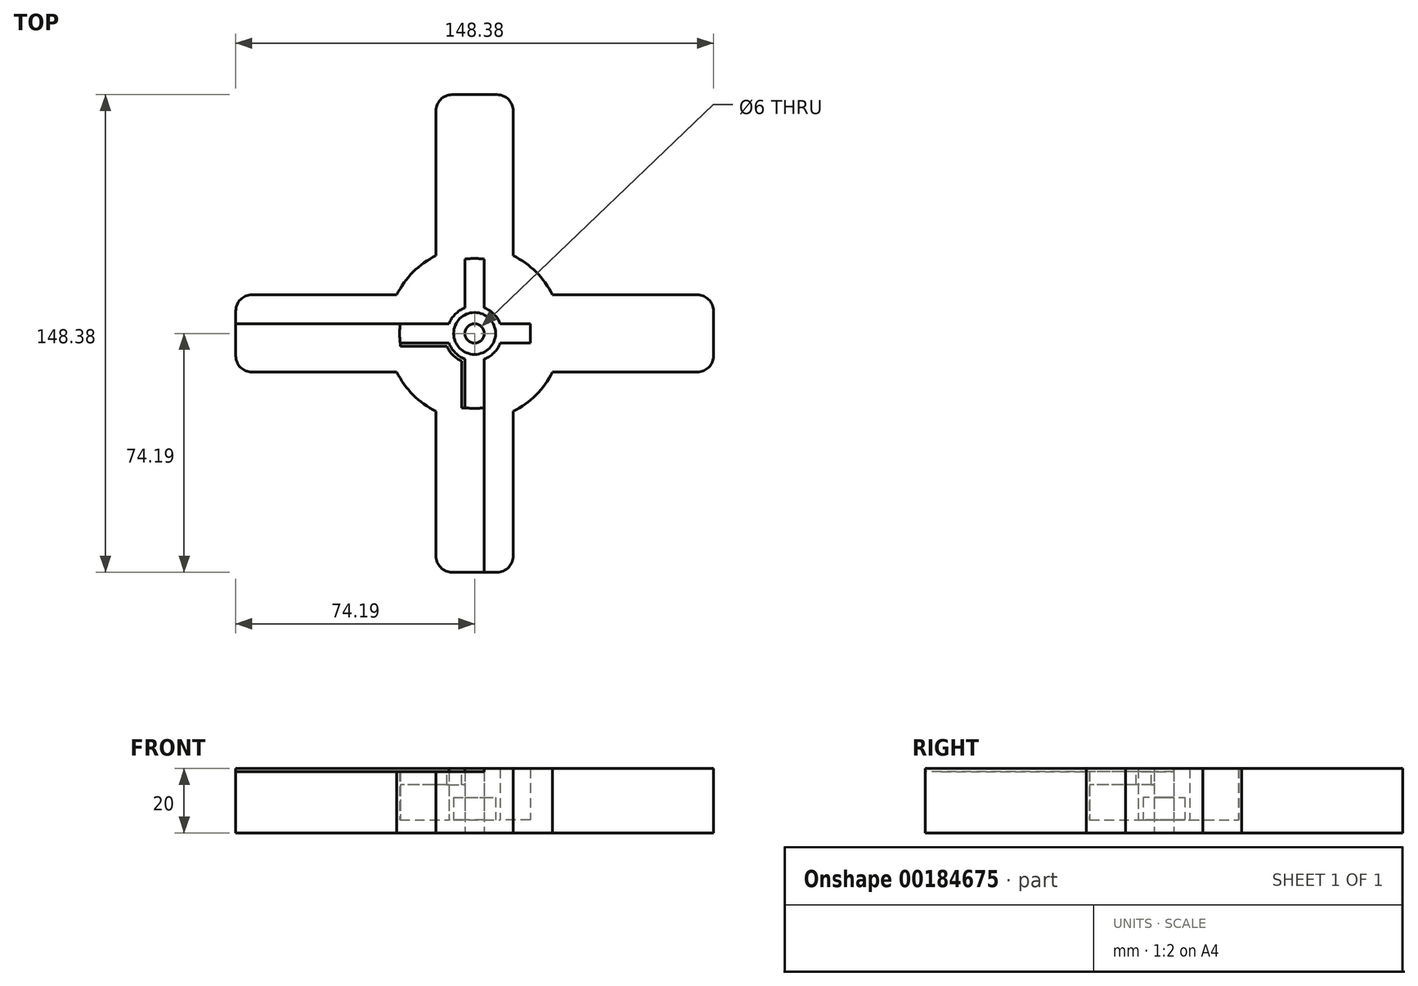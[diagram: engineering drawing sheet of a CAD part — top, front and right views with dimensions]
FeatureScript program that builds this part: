
annotation { "Feature Type Name" : "Feature", "Feature Type Description" : "" }
export const myFeature = defineFeature(function(context is Context, id is Id, definition is map)
    precondition{}
    {
        {
            var Q0;
            Q0=qCreatedBy(makeId("Top.planeOp"),FACE);
            var sketch = newSketch(context, id + "F0", { "sketchPlane" : qUnion([Q0])});
            skCircle(sketch, "E0", {"center": v(0, 0) * mm, "radius": 27 * mm});
            skCircle(sketch, "E1", {"center": v(0, 0) * mm, "radius": 23.3 * mm});
            skLineSegment(sketch, "E2", {"start": v(-3, 33.88) * mm, "end": v(-3, -40.65) * mm, "construction": true});
            skLineSegment(sketch, "E3", {"start": v(-3, -40.65) * mm, "end": v(3, -40.65) * mm, "construction": true});
            skLineSegment(sketch, "E4", {"start": v(3, -40.65) * mm, "end": v(3, 33.88) * mm, "construction": true});
            skLineSegment(sketch, "E5", {"start": v(3, 33.88) * mm, "end": v(-3, 33.88) * mm, "construction": true});
            skCircle(sketch, "E6", {"center": v(0, 0) * mm, "radius": 8.5 * mm, "construction": true});
            skCircle(sketch, "E7", {"center": v(0, 0) * mm, "radius": 6 * mm, "construction": true});
            skCircle(sketch, "E8", {"center": v(0, 0) * mm, "radius": 3 * mm});
            skLineSegment(sketch, "E9", {"start": v(-37.32, -3) * mm, "end": v(17.3, -3) * mm, "construction": true});
            skLineSegment(sketch, "E10", {"start": v(17.3, -3) * mm, "end": v(17.3, 3) * mm, "construction": true});
            skLineSegment(sketch, "E11", {"start": v(17.3, 3) * mm, "end": v(-37.32, 3) * mm, "construction": true});
            skLineSegment(sketch, "E12", {"start": v(-37.32, 3) * mm, "end": v(-37.32, -3) * mm, "construction": true});
            skLineSegment(sketch, "E13", {"start": v(-23.1, 3) * mm, "end": v(-7.95, 3) * mm});
            skPoint(sketch, "E13.endSnap0", {"position": v(-10, 3) * mm});
            skLineSegment(sketch, "E14", {"start": v(-3, 23.1) * mm, "end": v(-3, 7.95) * mm});
            skLineSegment(sketch, "E15", {"start": v(3, 23.1) * mm, "end": v(3, 7.95) * mm});
            skLineSegment(sketch, "E16", {"start": v(7.95, 3) * mm, "end": v(17.3, 3) * mm});
            skLineSegment(sketch, "E17", {"start": v(7.95, -3) * mm, "end": v(17.3, -3) * mm});
            skLineSegment(sketch, "E18", {"start": v(17.3, -3) * mm, "end": v(17.3, 3) * mm});
            skLineSegment(sketch, "E19", {"start": v(3, -7.95) * mm, "end": v(3, -23.1) * mm});
            skLineSegment(sketch, "E20", {"start": v(-3, -7.95) * mm, "end": v(-3, -23.1) * mm});
            skLineSegment(sketch, "E21", {"start": v(-7.95, -3) * mm, "end": v(-23.1, -3) * mm});
            skArc(sketch, "E22", {"start": v(-7.95, 3) * mm, "mid": v(-6.01, 6.01) * mm, "end": v(-3, 7.95) * mm});
            skArc(sketch, "E23", {"start": v(3, 7.95) * mm, "mid": v(6.01, 6.01) * mm, "end": v(7.95, 3) * mm});
            skArc(sketch, "E24", {"start": v(7.95, -3) * mm, "mid": v(6.01, -6.01) * mm, "end": v(3, -7.95) * mm});
            skArc(sketch, "E25", {"start": v(-3, -7.95) * mm, "mid": v(-6.01, -6.01) * mm, "end": v(-7.95, -3) * mm});
            skLineSegment(sketch, "E26", {"start": v(-7, -74.19) * mm, "end": v(7, -74.19) * mm, "construction": true});
            skLineSegment(sketch, "E27", {"start": v(7, 74.19) * mm, "end": v(-7, 74.19) * mm, "construction": true});
            skLineSegment(sketch, "E28", {"start": v(74.19, 7) * mm, "end": v(74.19, -7) * mm, "construction": true});
            skLineSegment(sketch, "E29", {"start": v(-74.19, -7) * mm, "end": v(-74.19, 7) * mm, "construction": true});
            skLineSegment(sketch, "E30", {"start": v(-24.19, 12) * mm, "end": v(-69.19, 12) * mm});
            skLineSegment(sketch, "E31", {"start": v(-74.19, -12) * mm, "end": v(-74.19, 12) * mm});
            skLineSegment(sketch, "E32", {"start": v(-69.19, -12) * mm, "end": v(-24.19, -12) * mm});
            skLineSegment(sketch, "E33", {"start": v(24.19, -12) * mm, "end": v(69.19, -12) * mm});
            skLineSegment(sketch, "E34", {"start": v(74.19, -12) * mm, "end": v(74.19, 12) * mm});
            skLineSegment(sketch, "E35", {"start": v(24.19, 12) * mm, "end": v(69.19, 12) * mm});
            skLineSegment(sketch, "E36", {"start": v(12, -24.19) * mm, "end": v(12, -69.19) * mm});
            skLineSegment(sketch, "E37", {"start": v(12, -74.19) * mm, "end": v(-12, -74.19) * mm});
            skLineSegment(sketch, "E38", {"start": v(-12, -69.19) * mm, "end": v(-12, -24.19) * mm});
            skLineSegment(sketch, "E39", {"start": v(-12, 24.19) * mm, "end": v(-12, 69.19) * mm});
            skLineSegment(sketch, "E40", {"start": v(-12, 74.19) * mm, "end": v(12, 74.19) * mm});
            skLineSegment(sketch, "E41", {"start": v(12, 69.19) * mm, "end": v(12, 24.19) * mm});
            skPoint(sketch, "E42.visualSharp", {"position": v(-74.19, 12) * mm});
            skArc(sketch, "E42.filletArc", {"start": v(-69.19, 12) * mm, "mid": v(-72.72, 10.54) * mm, "end": v(-74.19, 7) * mm});
            skPoint(sketch, "E43.visualSharp", {"position": v(-74.19, -12) * mm});
            skArc(sketch, "E43.filletArc", {"start": v(-74.19, -7) * mm, "mid": v(-72.72, -10.54) * mm, "end": v(-69.19, -12) * mm});
            skPoint(sketch, "E44.visualSharp", {"position": v(74.19, -12) * mm});
            skArc(sketch, "E44.filletArc", {"start": v(69.19, -12) * mm, "mid": v(72.72, -10.54) * mm, "end": v(74.19, -7) * mm});
            skPoint(sketch, "E45.visualSharp", {"position": v(74.19, 12) * mm});
            skArc(sketch, "E45.filletArc", {"start": v(74.19, 7) * mm, "mid": v(72.72, 10.54) * mm, "end": v(69.19, 12) * mm});
            skPoint(sketch, "E46.visualSharp", {"position": v(12, -74.19) * mm});
            skArc(sketch, "E46.filletArc", {"start": v(7, -74.19) * mm, "mid": v(10.54, -72.72) * mm, "end": v(12, -69.19) * mm});
            skPoint(sketch, "E47.visualSharp", {"position": v(-12, -74.19) * mm});
            skArc(sketch, "E47.filletArc", {"start": v(-12, -69.19) * mm, "mid": v(-10.54, -72.72) * mm, "end": v(-7, -74.19) * mm});
            skPoint(sketch, "E48.visualSharp", {"position": v(-12, 74.19) * mm});
            skArc(sketch, "E48.filletArc", {"start": v(-7, 74.19) * mm, "mid": v(-10.54, 72.72) * mm, "end": v(-12, 69.19) * mm});
            skPoint(sketch, "E49.visualSharp", {"position": v(12, 74.19) * mm});
            skArc(sketch, "E49.filletArc", {"start": v(12, 69.19) * mm, "mid": v(10.54, 72.72) * mm, "end": v(7, 74.19) * mm});
            skSolve(sketch);
        }
        {
            var Q0;
            {var subQ1=sQuery(id+"F0.wireOp",EDGE,"E30");Q0=makeQuery(id+"F0.imprint","IMPRINT",FACE,{"disambiguationData":[TD([[makeQuery(id+"F0.imprint","IMPRINT",EDGE,{"derivedFrom":subQ1}),1.0]])]});}
            var Q1;
            {var subQ0=sQuery(id+"F0.wireOp",EDGE,"E0");var subQ2=makeQuery(id+"F0.imprint","INTERSECT",VERTEX,{"derivedFrom":[subQ0,sQuery(id+"F0.wireOp",EDGE,"E35")]});Q1=makeQuery(id+"F0.imprint","IMPRINT",FACE,{"disambiguationData":[TD([[makeQuery(id+"F0.imprint","IMPRINT",EDGE,{"disambiguationData":[TD([[subQ2,-1.0]])],"derivedFrom":subQ0}),1.0]])]});}
            var Q2;
            {var subQ0=sQuery(id+"F0.wireOp",EDGE,"E13");Q2=makeQuery(id+"F0.imprint","IMPRINT",FACE,{"disambiguationData":[TD([[makeQuery(id+"F0.imprint","IMPRINT",EDGE,{"derivedFrom":subQ0}),1.0]])]});}
            var Q3;
            {var subQ0=sQuery(id+"F0.wireOp",EDGE,"E15");Q3=makeQuery(id+"F0.imprint","IMPRINT",FACE,{"disambiguationData":[TD([[makeQuery(id+"F0.imprint","IMPRINT",EDGE,{"derivedFrom":subQ0}),1.0]])]});}
            var Q4;
            {var subQ0=sQuery(id+"F0.wireOp",EDGE,"E20");Q4=makeQuery(id+"F0.imprint","IMPRINT",FACE,{"disambiguationData":[TD([[makeQuery(id+"F0.imprint","IMPRINT",EDGE,{"derivedFrom":subQ0}),-1.0]])]});}
            var Q5;
            {var subQ0=sQuery(id+"F0.wireOp",EDGE,"E39");Q5=makeQuery(id+"F0.imprint","IMPRINT",FACE,{"disambiguationData":[TD([[makeQuery(id+"F0.imprint","IMPRINT",EDGE,{"derivedFrom":subQ0}),-1.0]])]});}
            var Q6;
            {var subQ4=sQuery(id+"F0.wireOp",EDGE,"E33");Q6=makeQuery(id+"F0.imprint","IMPRINT",FACE,{"disambiguationData":[TD([[makeQuery(id+"F0.imprint","IMPRINT",EDGE,{"derivedFrom":subQ4}),1.0]])]});}
            var Q7;
            {var subQ1=sQuery(id+"F0.wireOp",EDGE,"E36");Q7=makeQuery(id+"F0.imprint","IMPRINT",FACE,{"disambiguationData":[TD([[makeQuery(id+"F0.imprint","IMPRINT",EDGE,{"derivedFrom":subQ1}),-1.0]])]});}
            extrude(context, id + "F1", {"entities" : qUnion([Q0, Q1, Q2, Q3, Q4, Q5, Q6, Q7]), "depth" : 20 * mm});
        }
        {
            var Q0;
            Q0=makeQuery(id+"F1.opExtrude","CAP_FACE",FACE,{"disambiguationData":[OSD([sQuery(id+"F0.wireOp",EDGE,"E0"),sQuery(id+"F0.wireOp",EDGE,"E1"),sQuery(id+"F0.wireOp",EDGE,"E13"),sQuery(id+"F0.wireOp",EDGE,"E14"),sQuery(id+"F0.wireOp",EDGE,"E15"),sQuery(id+"F0.wireOp",EDGE,"E16"),sQuery(id+"F0.wireOp",EDGE,"E17"),sQuery(id+"F0.wireOp",EDGE,"E18"),sQuery(id+"F0.wireOp",EDGE,"E19"),sQuery(id+"F0.wireOp",EDGE,"E20"),sQuery(id+"F0.wireOp",EDGE,"E21"),sQuery(id+"F0.wireOp",EDGE,"E22"),sQuery(id+"F0.wireOp",EDGE,"E23"),sQuery(id+"F0.wireOp",EDGE,"E24"),sQuery(id+"F0.wireOp",EDGE,"E25"),sQuery(id+"F0.wireOp",EDGE,"E30"),sQuery(id+"F0.wireOp",EDGE,"E31"),sQuery(id+"F0.wireOp",EDGE,"E32"),sQuery(id+"F0.wireOp",EDGE,"E33"),sQuery(id+"F0.wireOp",EDGE,"E34"),sQuery(id+"F0.wireOp",EDGE,"E35"),sQuery(id+"F0.wireOp",EDGE,"E36"),sQuery(id+"F0.wireOp",EDGE,"E37"),sQuery(id+"F0.wireOp",EDGE,"E38"),sQuery(id+"F0.wireOp",EDGE,"E39"),sQuery(id+"F0.wireOp",EDGE,"E40"),sQuery(id+"F0.wireOp",EDGE,"E41"),sQuery(id+"F0.wireOp",EDGE,"E42.filletArc"),sQuery(id+"F0.wireOp",EDGE,"E43.filletArc"),sQuery(id+"F0.wireOp",EDGE,"E44.filletArc"),sQuery(id+"F0.wireOp",EDGE,"E45.filletArc"),sQuery(id+"F0.wireOp",EDGE,"E46.filletArc"),sQuery(id+"F0.wireOp",EDGE,"E47.filletArc"),sQuery(id+"F0.wireOp",EDGE,"E48.filletArc"),sQuery(id+"F0.wireOp",EDGE,"E49.filletArc")])],"isStart":false});
            var sketch = newSketch(context, id + "F2", { "sketchPlane" : qUnion([Q0])});
            skLineSegment(sketch, "E50", {"start": v(3, -23.1) * mm, "end": v(3, -74.19) * mm});
            skLineSegment(sketch, "E51", {"start": v(-23.1, 3) * mm, "end": v(-74.19, 3) * mm});
            skSolve(sketch);
        }
        {
            var Q0;
            {var subQ7=sQuery(id+"F2.wireOp",EDGE,"E50");Q0=makeQuery(id+"F2.imprint","IMPRINT",FACE,{"disambiguationData":[TD([[makeQuery(id+"F2.imprint","IMPRINT",EDGE,{"derivedFrom":subQ7}),-1.0]])]});}
            extrude(context, id + "F3", {"entities" : qUnion([Q0]), "operationType" : NewBodyOperationType.REMOVE, "oppositeDirection" : true, "depth" : 1 * mm});
        }
        {
            var Q0;
            Q0=makeQuery(id+"F3.boolean.opBoolean","COPY",FACE,{"derivedFrom":makeQuery(id+"F3.opExtrude","CAP_FACE",FACE,{"disambiguationData":[OSD([sQuery(id+"F0.wireOp",EDGE,"E0"),sQuery(id+"F0.wireOp",EDGE,"E1"),sQuery(id+"F0.wireOp",EDGE,"E20"),sQuery(id+"F0.wireOp",EDGE,"E21"),sQuery(id+"F0.wireOp",EDGE,"E25"),sQuery(id+"F0.wireOp",EDGE,"E31"),sQuery(id+"F0.wireOp",EDGE,"E32"),sQuery(id+"F0.wireOp",EDGE,"E37"),sQuery(id+"F0.wireOp",EDGE,"E38"),sQuery(id+"F0.wireOp",EDGE,"E43.filletArc"),sQuery(id+"F0.wireOp",EDGE,"E47.filletArc"),sQuery(id+"F2.wireOp",EDGE,"E50"),sQuery(id+"F2.wireOp",EDGE,"E51")])],"isStart":false})});
            var sketch = newSketch(context, id + "F4", { "sketchPlane" : qUnion([Q0])});
            skLineSegment(sketch, "E52.0", {"start": v(-4, -8.62) * mm, "end": v(-4, -23.1) * mm});
            skArc(sketch, "E52.1", {"start": v(-4, -8.62) * mm, "mid": v(-6.72, -6.72) * mm, "end": v(-8.62, -4) * mm});
            skLineSegment(sketch, "E52.2", {"start": v(-8.62, -4) * mm, "end": v(-23.1, -4) * mm});
            skLineSegment(sketch, "E53", {"start": v(-3, -23.1) * mm, "end": v(-4, -23.1) * mm});
            skLineSegment(sketch, "E54", {"start": v(-23.1, -4) * mm, "end": v(-23.1, -3) * mm});
            skSolve(sketch);
        }
        {
            var Q0;
            Q0=makeQuery(id+"F4.imprint","IMPRINT",FACE,{"disambiguationData":[TD([[makeQuery(id+"F4.imprint","IMPRINT",EDGE,{"derivedFrom":sQuery(id+"F4.wireOp",EDGE,"E52.0")}),1.0]])]});
            extrude(context, id + "F5", {"entities" : qUnion([Q0]), "operationType" : NewBodyOperationType.REMOVE, "oppositeDirection" : true, "depth" : 4 * mm});
        }
        {
            var Q0;
            Q0=makeQuery(id+"F1.opExtrude","CAP_FACE",FACE,{"disambiguationData":[OSD([sQuery(id+"F0.wireOp",EDGE,"E0"),sQuery(id+"F0.wireOp",EDGE,"E1"),sQuery(id+"F0.wireOp",EDGE,"E13"),sQuery(id+"F0.wireOp",EDGE,"E14"),sQuery(id+"F0.wireOp",EDGE,"E15"),sQuery(id+"F0.wireOp",EDGE,"E16"),sQuery(id+"F0.wireOp",EDGE,"E17"),sQuery(id+"F0.wireOp",EDGE,"E18"),sQuery(id+"F0.wireOp",EDGE,"E19"),sQuery(id+"F0.wireOp",EDGE,"E20"),sQuery(id+"F0.wireOp",EDGE,"E21"),sQuery(id+"F0.wireOp",EDGE,"E22"),sQuery(id+"F0.wireOp",EDGE,"E23"),sQuery(id+"F0.wireOp",EDGE,"E24"),sQuery(id+"F0.wireOp",EDGE,"E25"),sQuery(id+"F0.wireOp",EDGE,"E30"),sQuery(id+"F0.wireOp",EDGE,"E31"),sQuery(id+"F0.wireOp",EDGE,"E32"),sQuery(id+"F0.wireOp",EDGE,"E33"),sQuery(id+"F0.wireOp",EDGE,"E34"),sQuery(id+"F0.wireOp",EDGE,"E35"),sQuery(id+"F0.wireOp",EDGE,"E36"),sQuery(id+"F0.wireOp",EDGE,"E37"),sQuery(id+"F0.wireOp",EDGE,"E38"),sQuery(id+"F0.wireOp",EDGE,"E39"),sQuery(id+"F0.wireOp",EDGE,"E40"),sQuery(id+"F0.wireOp",EDGE,"E41"),sQuery(id+"F0.wireOp",EDGE,"E42.filletArc"),sQuery(id+"F0.wireOp",EDGE,"E43.filletArc"),sQuery(id+"F0.wireOp",EDGE,"E44.filletArc"),sQuery(id+"F0.wireOp",EDGE,"E45.filletArc"),sQuery(id+"F0.wireOp",EDGE,"E46.filletArc"),sQuery(id+"F0.wireOp",EDGE,"E47.filletArc"),sQuery(id+"F0.wireOp",EDGE,"E48.filletArc"),sQuery(id+"F0.wireOp",EDGE,"E49.filletArc")])],"isStart":true});
            var sketch = newSketch(context, id + "F6", { "sketchPlane" : qUnion([Q0])});
            skCircle(sketch, "E55", {"center": v(0, 0) * mm, "radius": 3 * mm});
            skSolve(sketch);
        }
        {
            var Q0;
            {var subQ15=sQuery(id+"F0.wireOp",EDGE,"E13");Q0=makeQuery(id+"F6.imprint","IMPRINT",FACE,{"disambiguationData":[TD([[makeQuery(id+"F6.imprint","IMPRINT",EDGE,{"derivedFrom":makeQuery(id+"F1.opExtrude","CAP_EDGE",EDGE,{"disambiguationData":[OSD([subQ15])],"isStart":true})}),-1.0]])]});}
            var Q1;
            Q1=makeQuery(id+"F6.imprint","IMPRINT",FACE,{"disambiguationData":[TD([[makeQuery(id+"F6.imprint","IMPRINT",EDGE,{"derivedFrom":sQuery(id+"F6.wireOp",EDGE,"E55")}),-1.0]])]});
            extrude(context, id + "F7", {"entities" : qUnion([Q0, Q1]), "operationType" : NewBodyOperationType.ADD, "oppositeDirection" : true, "depth" : 4 * mm});
        }
        {
            var Q0;
            Q0=makeQuery(id+"F7.opExtrude","CAP_FACE",FACE,{"disambiguationData":[OSD([sQuery(id+"F0.wireOp",EDGE,"E0"),sQuery(id+"F0.wireOp",EDGE,"E30"),sQuery(id+"F0.wireOp",EDGE,"E31"),sQuery(id+"F0.wireOp",EDGE,"E32"),sQuery(id+"F0.wireOp",EDGE,"E33"),sQuery(id+"F0.wireOp",EDGE,"E34"),sQuery(id+"F0.wireOp",EDGE,"E35"),sQuery(id+"F0.wireOp",EDGE,"E36"),sQuery(id+"F0.wireOp",EDGE,"E37"),sQuery(id+"F0.wireOp",EDGE,"E38"),sQuery(id+"F0.wireOp",EDGE,"E39"),sQuery(id+"F0.wireOp",EDGE,"E40"),sQuery(id+"F0.wireOp",EDGE,"E41"),sQuery(id+"F0.wireOp",EDGE,"E42.filletArc"),sQuery(id+"F0.wireOp",EDGE,"E43.filletArc"),sQuery(id+"F0.wireOp",EDGE,"E44.filletArc"),sQuery(id+"F0.wireOp",EDGE,"E45.filletArc"),sQuery(id+"F0.wireOp",EDGE,"E46.filletArc"),sQuery(id+"F0.wireOp",EDGE,"E47.filletArc"),sQuery(id+"F0.wireOp",EDGE,"E48.filletArc"),sQuery(id+"F0.wireOp",EDGE,"E49.filletArc"),sQuery(id+"F6.wireOp",EDGE,"E55")])],"isStart":false});
            var sketch = newSketch(context, id + "F8", { "sketchPlane" : qUnion([Q0])});
            skCircle(sketch, "E56", {"center": v(0, 0) * mm, "radius": 6.5 * mm});
            skSolve(sketch);
        }
        {
            var Q0;
            Q0=makeQuery(id+"F8.imprint","IMPRINT",FACE,{"disambiguationData":[TD([[makeQuery(id+"F8.imprint","IMPRINT",EDGE,{"derivedFrom":sQuery(id+"F8.wireOp",EDGE,"E56")}),1.0]])]});
            extrude(context, id + "F9", {"entities" : qUnion([Q0]), "operationType" : NewBodyOperationType.ADD, "depth" : 7 * mm});
        }
    });
